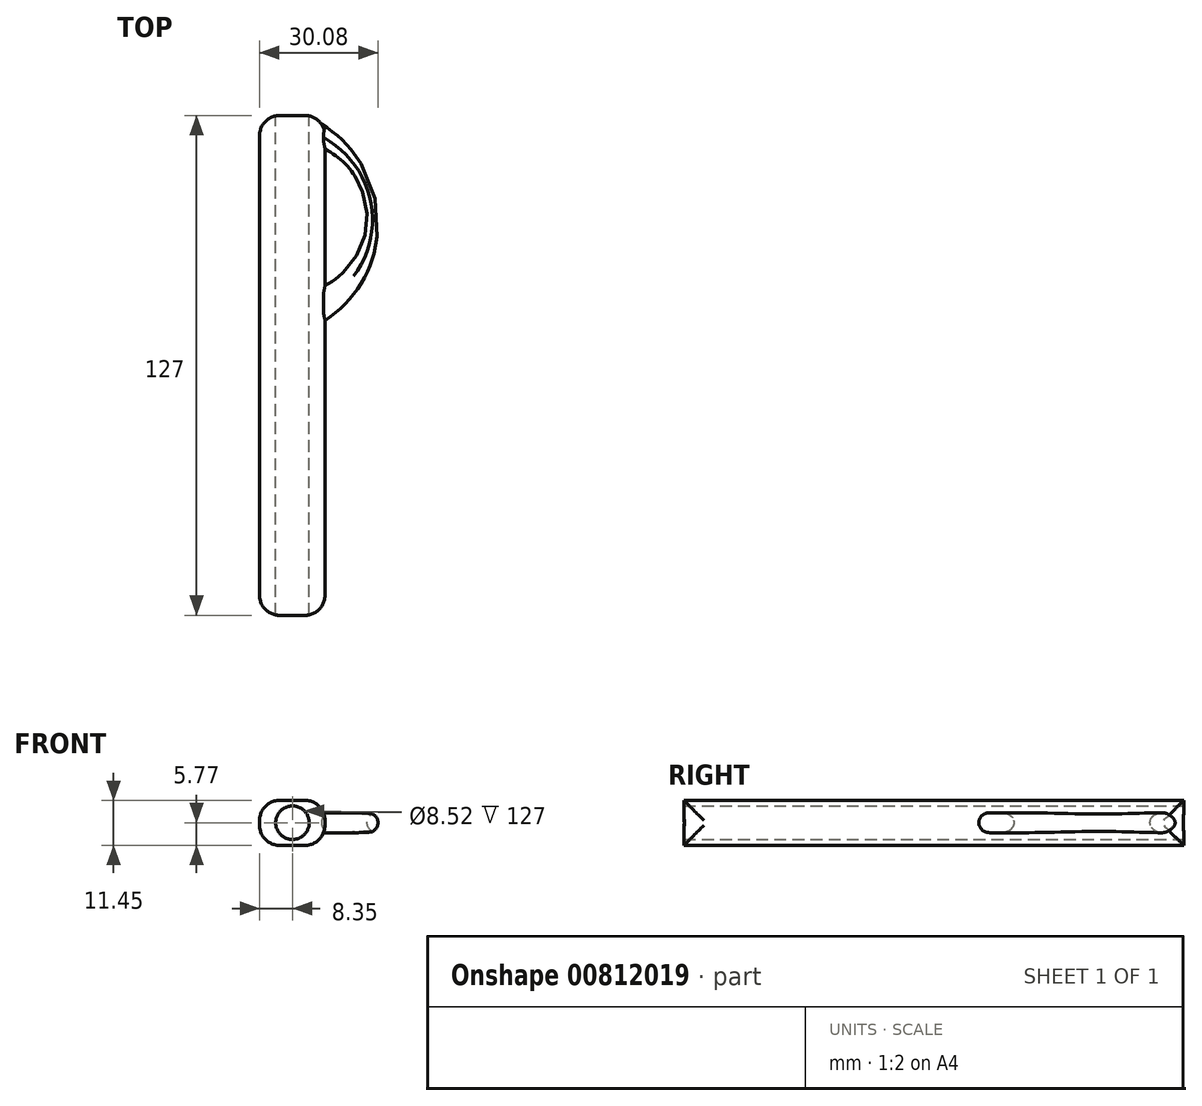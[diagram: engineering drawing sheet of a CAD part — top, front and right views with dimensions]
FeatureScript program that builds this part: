
annotation { "Feature Type Name" : "Feature", "Feature Type Description" : "" }
export const myFeature = defineFeature(function(context is Context, id is Id, definition is map)
    precondition{}
    {
        {
            var Q0;
            Q0=qCreatedBy(makeId("Front.planeOp"),FACE);
            var sketch = newSketch(context, id + "F0", { "sketchPlane" : qUnion([Q0])});
            skCircle(sketch, "E0", {"center": v(0, 0) * mm, "radius": 4.26 * mm});
            skLineSegment(sketch, "E1.bottom", {"start": v(8.26, 5.68) * mm, "end": v(-8.35, 5.68) * mm});
            skLineSegment(sketch, "E1.top", {"start": v(8.26, -5.77) * mm, "end": v(-8.35, -5.77) * mm});
            skLineSegment(sketch, "E1.left", {"start": v(8.26, 5.68) * mm, "end": v(8.26, -5.77) * mm});
            skLineSegment(sketch, "E1.right", {"start": v(-8.35, 5.68) * mm, "end": v(-8.35, -5.77) * mm});
            skSolve(sketch);
        }
        {
            var Q0;
            Q0=makeQuery(id+"F0.imprint","IMPRINT",FACE,{"disambiguationData":[TD([[makeQuery(id+"F0.imprint","IMPRINT",EDGE,{"derivedFrom":sQuery(id+"F0.wireOp",EDGE,"E0")}),-1.0]])]});
            extrude(context, id + "F1", {"entities" : qUnion([Q0]), "depth" : 127 * mm, "offsetDistance" : 25.4 * mm});
        }
        {
            var Q0;
            Q0=makeQuery(id+"F1.opExtrude","SWEPT_EDGE",EDGE,{"disambiguationData":[OSD([sQuery(id+"F0.wireOp",EDGE,"E1.bottom"),sQuery(id+"F0.wireOp",EDGE,"E1.left")])]});
            var Q1;
            Q1=makeQuery(id+"F1.opExtrude","SWEPT_FACE",FACE,{"disambiguationData":[OSD([sQuery(id+"F0.wireOp",EDGE,"E1.left")])]});
            var Q2;
            Q2=makeQuery(id+"F1.opExtrude","SWEPT_FACE",FACE,{"disambiguationData":[OSD([sQuery(id+"F0.wireOp",EDGE,"E1.right")])]});
            fillet(context, id + "F2", {"entities" : qUnion([Q0, Q1, Q2]), "radius" : 5.08 * mm, "tangentPropagation" : true, "allowEdgeOverflow" : false});
        }
        {
            var Q0;
            Q0=qCreatedBy(makeId("Top.planeOp"),FACE);
            var sketch = newSketch(context, id + "F3", { "sketchPlane" : qUnion([Q0])});
            skArc(sketch, "E2", {"start": v(6.93, -43.76) * mm, "mid": v(18.95, -25.33) * mm, "end": v(5.94, -7.58) * mm});
            skArc(sketch, "E3", {"start": v(6.73, -53) * mm, "mid": v(21.73, -27.44) * mm, "end": v(6.8, -1.86) * mm});
            skLineSegment(sketch, "E4", {"start": v(6.73, -53) * mm, "end": v(6.93, -43.76) * mm});
            skLineSegment(sketch, "E5", {"start": v(5.94, -7.58) * mm, "end": v(6.8, -1.86) * mm});
            skSolve(sketch);
        }
        {
            var Q0;
            Q0=makeQuery(id+"F3.imprint","IMPRINT",FACE,{"disambiguationData":[TD([[makeQuery(id+"F3.imprint","IMPRINT",EDGE,{"derivedFrom":sQuery(id+"F3.wireOp",EDGE,"E2")}),-1.0]])]});
            extrude(context, id + "F4", {"entities" : qUnion([Q0]), "operationType" : NewBodyOperationType.ADD, "depth" : 2.54 * mm, "offsetDistance" : 25.4 * mm, "hasSecondDirection" : true, "secondDirectionOppositeDirection" : true, "secondDirectionDepth" : 2.54 * mm});
        }
        {
            var Q0;
            Q0=makeQuery(id+"F4.opExtrude","CAP_EDGE",EDGE,{"disambiguationData":[OSD([sQuery(id+"F3.wireOp",EDGE,"E3")])],"isStart":false});
            var Q1;
            Q1=makeQuery(id+"F4.opExtrude","CAP_EDGE",EDGE,{"disambiguationData":[OSD([sQuery(id+"F3.wireOp",EDGE,"E3")])],"isStart":true});
            fillet(context, id + "F5", {"entities" : qUnion([Q0, Q1]), "radius" : 2.54 * mm, "tangentPropagation" : true, "allowEdgeOverflow" : false});
        }
        {
            var Q0;
            Q0=makeQuery(id+"F4.opExtrude","CAP_EDGE",EDGE,{"disambiguationData":[OSD([sQuery(id+"F3.wireOp",EDGE,"E2")])],"isStart":false});
            var Q1;
            Q1=makeQuery(id+"F4.opExtrude","CAP_EDGE",EDGE,{"disambiguationData":[OSD([sQuery(id+"F3.wireOp",EDGE,"E2")])],"isStart":true});
            fillet(context, id + "F6", {"entities" : qUnion([Q0, Q1]), "radius" : 2.54 * mm, "tangentPropagation" : true, "allowEdgeOverflow" : false});
        }
    });
